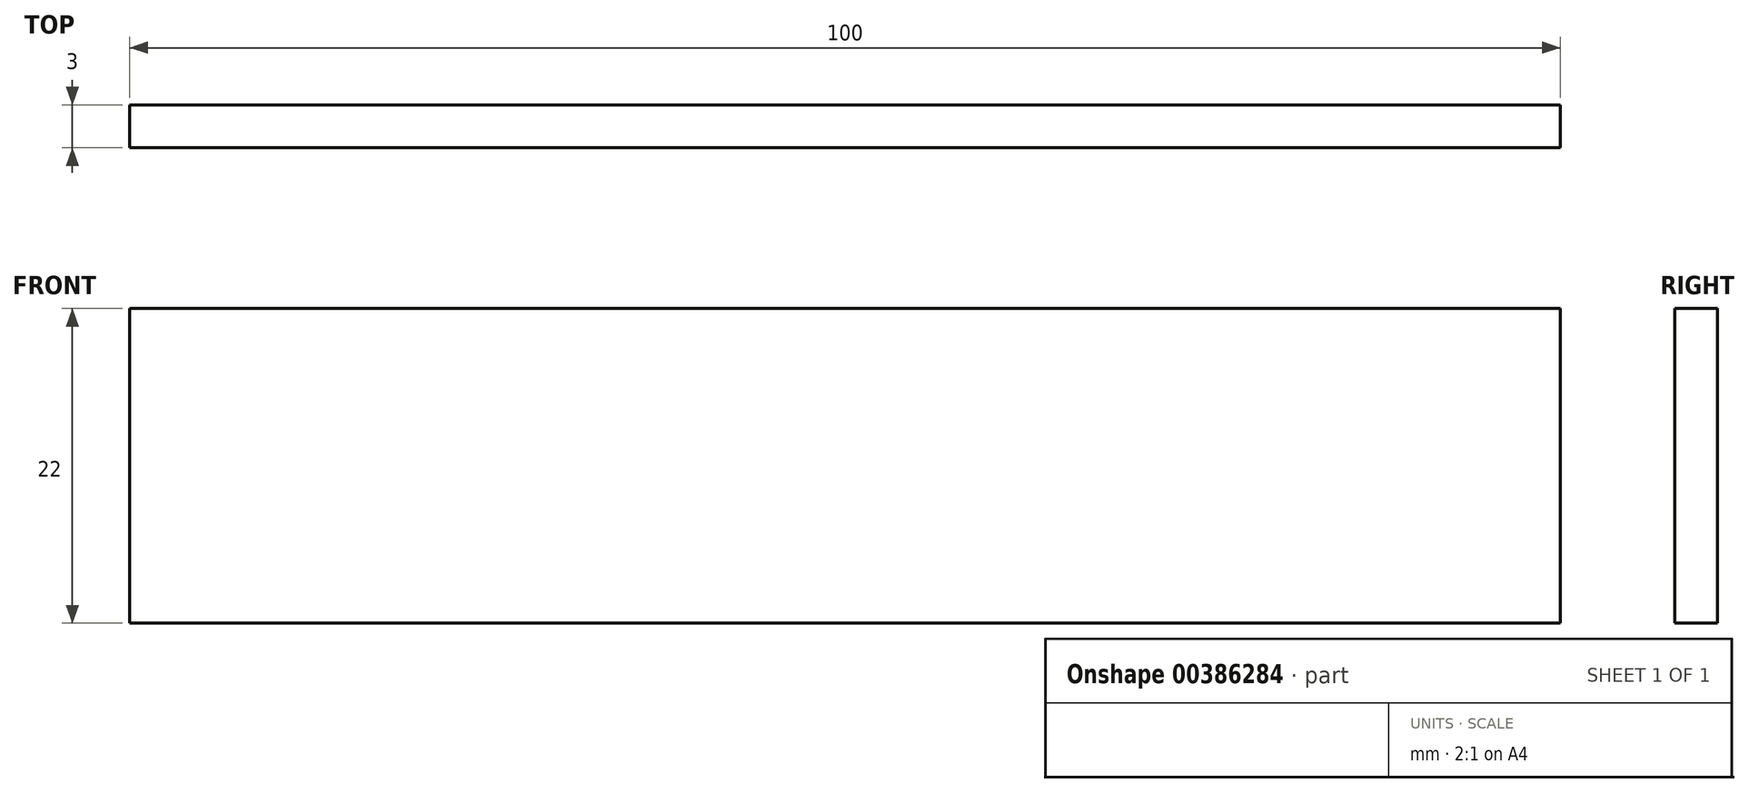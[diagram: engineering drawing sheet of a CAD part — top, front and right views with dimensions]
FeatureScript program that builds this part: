
annotation { "Feature Type Name" : "Feature", "Feature Type Description" : "" }
export const myFeature = defineFeature(function(context is Context, id is Id, definition is map)
    precondition{}
    {
        {
            var Q0;
            Q0=qCreatedBy(makeId("Front.planeOp"),FACE);
            var sketch = newSketch(context, id + "F0", { "sketchPlane" : qUnion([Q0])});
            skLineSegment(sketch, "E0.bottom", {"start": v(-42.1, 22.34) * mm, "end": v(57.9, 22.34) * mm});
            skLineSegment(sketch, "E0.top", {"start": v(-42.1, 0.34) * mm, "end": v(57.9, 0.34) * mm});
            skLineSegment(sketch, "E0.left", {"start": v(-42.1, 22.34) * mm, "end": v(-42.1, 0.34) * mm});
            skLineSegment(sketch, "E0.right", {"start": v(57.9, 22.34) * mm, "end": v(57.9, 0.34) * mm});
            skSolve(sketch);
        }
        {
            var Q0;
            Q0=makeQuery(id+"F0.imprint","IMPRINT",FACE,{"disambiguationData":[TD([[makeQuery(id+"F0.imprint","IMPRINT",EDGE,{"derivedFrom":sQuery(id+"F0.wireOp",EDGE,"E0.bottom")}),-1.0]])]});
            extrude(context, id + "F1", {"entities" : qUnion([Q0]), "depth" : 3 * mm});
        }
    });
